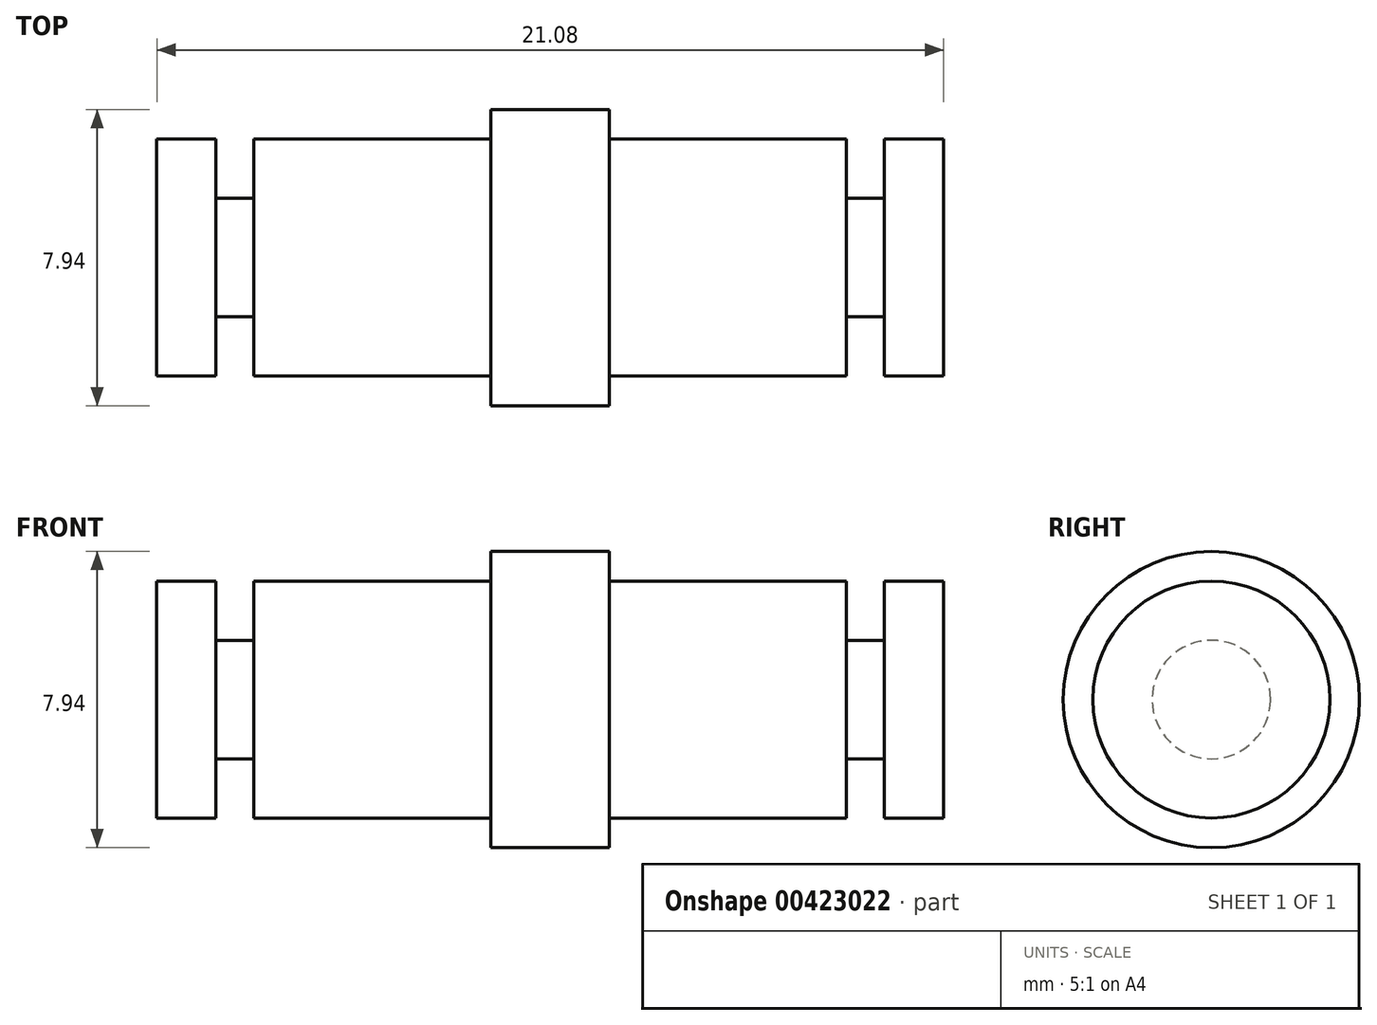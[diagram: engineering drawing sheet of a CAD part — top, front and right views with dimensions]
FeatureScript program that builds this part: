
annotation { "Feature Type Name" : "Feature", "Feature Type Description" : "" }
export const myFeature = defineFeature(function(context is Context, id is Id, definition is map)
    precondition{}
    {
        {
            var Q0;
            Q0=qCreatedBy(makeId("Top.planeOp"),FACE);
            var sketch = newSketch(context, id + "F0", { "sketchPlane" : qUnion([Q0])});
            skLineSegment(sketch, "E0.bottom", {"start": v(-16.11, 0) * mm, "end": v(-14.52, 0) * mm});
            skLineSegment(sketch, "E0.top", {"start": v(-16.11, 3.17) * mm, "end": v(-14.52, 3.17) * mm});
            skLineSegment(sketch, "E0.left", {"start": v(-16.11, 0) * mm, "end": v(-16.11, 3.17) * mm});
            skLineSegment(sketch, "E0.right", {"start": v(-14.52, 0) * mm, "end": v(-14.52, 3.17) * mm});
            skLineSegment(sketch, "E1.bottom", {"start": v(-14.52, 0) * mm, "end": v(-13.5, 0) * mm});
            skLineSegment(sketch, "E1.top", {"start": v(-14.52, 1.59) * mm, "end": v(-13.5, 1.59) * mm});
            skLineSegment(sketch, "E1.left", {"start": v(-14.52, 0) * mm, "end": v(-14.52, 1.59) * mm});
            skLineSegment(sketch, "E1.right", {"start": v(-13.5, 0) * mm, "end": v(-13.5, 1.59) * mm});
            skLineSegment(sketch, "E2.bottom", {"start": v(-13.5, 0) * mm, "end": v(-7.16, 0) * mm});
            skLineSegment(sketch, "E2.top", {"start": v(-13.5, 3.17) * mm, "end": v(-7.16, 3.17) * mm});
            skLineSegment(sketch, "E2.left", {"start": v(-13.5, 0) * mm, "end": v(-13.5, 3.17) * mm});
            skLineSegment(sketch, "E2.right", {"start": v(-7.16, 0) * mm, "end": v(-7.16, 3.17) * mm});
            skLineSegment(sketch, "E3.bottom", {"start": v(-7.16, 0) * mm, "end": v(-3.98, 0) * mm});
            skLineSegment(sketch, "E3.top", {"start": v(-7.16, 3.97) * mm, "end": v(-3.98, 3.97) * mm});
            skLineSegment(sketch, "E3.left", {"start": v(-7.16, 0) * mm, "end": v(-7.16, 3.97) * mm});
            skLineSegment(sketch, "E3.right", {"start": v(-3.98, 0) * mm, "end": v(-3.98, 3.97) * mm});
            skLineSegment(sketch, "E4.bottom", {"start": v(-3.98, 0) * mm, "end": v(2.37, 0) * mm});
            skLineSegment(sketch, "E4.top", {"start": v(-3.98, 3.17) * mm, "end": v(2.37, 3.17) * mm});
            skLineSegment(sketch, "E4.left", {"start": v(-3.98, 0) * mm, "end": v(-3.98, 3.17) * mm});
            skLineSegment(sketch, "E4.right", {"start": v(2.37, 0) * mm, "end": v(2.37, 3.17) * mm});
            skLineSegment(sketch, "E5.bottom", {"start": v(2.37, 0) * mm, "end": v(3.38, 0) * mm});
            skLineSegment(sketch, "E5.top", {"start": v(2.37, 1.59) * mm, "end": v(3.38, 1.59) * mm});
            skLineSegment(sketch, "E5.left", {"start": v(2.37, 0) * mm, "end": v(2.37, 1.59) * mm});
            skLineSegment(sketch, "E5.right", {"start": v(3.38, 0) * mm, "end": v(3.38, 1.59) * mm});
            skLineSegment(sketch, "E6.bottom", {"start": v(3.38, 0) * mm, "end": v(4.97, 0) * mm});
            skLineSegment(sketch, "E6.top", {"start": v(3.38, 3.18) * mm, "end": v(4.97, 3.18) * mm});
            skLineSegment(sketch, "E6.left", {"start": v(3.38, 0) * mm, "end": v(3.38, 3.18) * mm});
            skLineSegment(sketch, "E6.right", {"start": v(4.97, 0) * mm, "end": v(4.97, 3.18) * mm});
            skSolve(sketch);
        }
        {
            var Q0;
            Q0=qSketchRegion(id+"F0",true);
            var Q1;
            Q1=sQuery(id+"F0.wireOp",EDGE,"E3.bottom");
            revolve(context, id + "F1", {"entities" : qUnion([Q0]), "axis" : qUnion([Q1]), "revolveType" : RevolveType.FULL});
        }
    });
